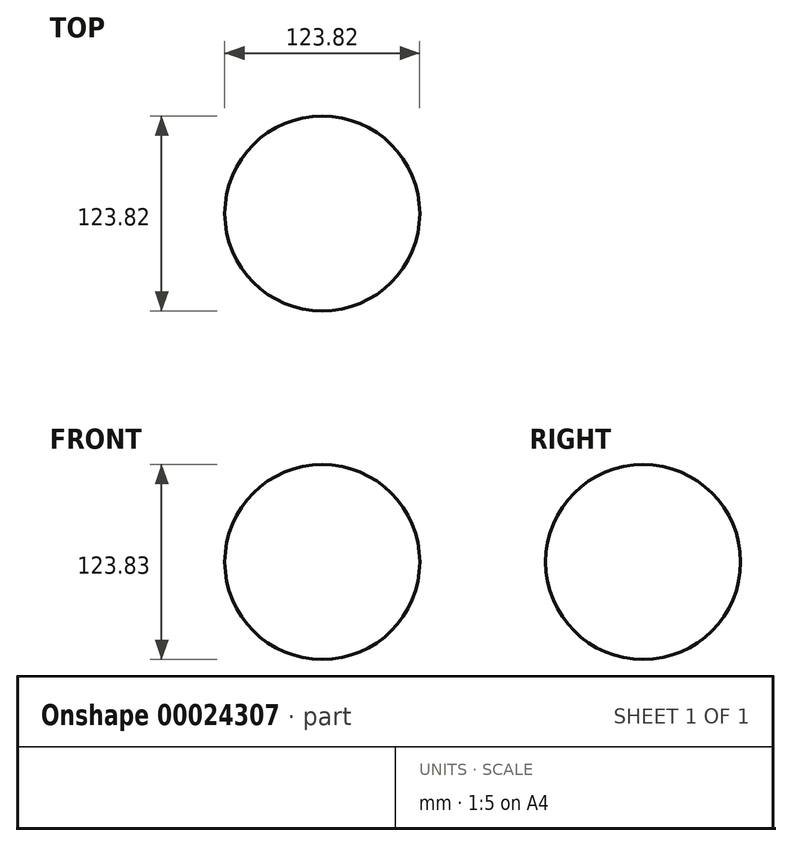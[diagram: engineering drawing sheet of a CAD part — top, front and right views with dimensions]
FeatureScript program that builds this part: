
annotation { "Feature Type Name" : "Feature", "Feature Type Description" : "" }
export const myFeature = defineFeature(function(context is Context, id is Id, definition is map)
    precondition{}
    {
        {
            var Q0;
            Q0=qCreatedBy(makeId("Right.planeOp"),FACE);
            var sketch = newSketch(context, id + "F0", { "sketchPlane" : qUnion([Q0])});
            skLineSegment(sketch, "E0", {"start": v(0, 0) * mm, "end": v(0, 123.83) * mm});
            skArc(sketch, "E1", {"start": v(0, 0) * mm, "mid": v(61.91, 61.91) * mm, "end": v(0, 123.83) * mm});
            skSolve(sketch);
        }
        {
            var Q0;
            Q0=makeQuery(id+"F0.imprint","IMPRINT",FACE,{"disambiguationData":[TD([[makeQuery(id+"F0.imprint","IMPRINT",EDGE,{"derivedFrom":sQuery(id+"F0.wireOp",EDGE,"E0")}),-1.0]])]});
            var Q1;
            Q1=sQuery(id+"F0.wireOp",EDGE,"E0");
            revolve(context, id + "F1", {"entities" : qUnion([Q0]), "axis" : qUnion([Q1]), "revolveType" : RevolveType.FULL});
        }
    });
